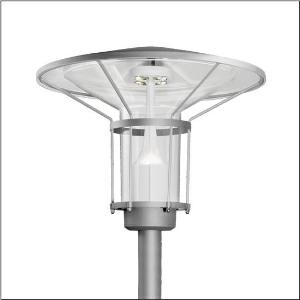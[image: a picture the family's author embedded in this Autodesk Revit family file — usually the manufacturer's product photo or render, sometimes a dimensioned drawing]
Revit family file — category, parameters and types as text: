
# Revit family: laterne_classic_iq___pl1_2s_5xa5245jf14h_d895
name_source: partatom
category: Lighting Fixtures
units: mm (PartAtom-declared; Revit-internal decimal feet)

## family parameters
Cut with Voids When Loaded = No
Host = Face
Light Source = No
Part Type = Normal
Room Calculation Point = No
Round Connector Dimension = Use Diameter
Shared = No

## types (1)
- --- (1 x LED, 2660 lm, 19.3 W, 3000K)
    Apparent Load = 19 VA
    CIE Flux Codes = 21 60 93 97 100
    Color Rendering = 70
    Color Temperature = 3000K
    Default Elevation = 1800 mm
    Description = Lantern Classic iQ, mast luminaire, Module 540 iQ-SR, primary light control with 3 zone facetted reflector, of plastic, silver coated, highly specular, structured, primary optical cover: cover, of PMMA, transparent, light distribution: PL1.2s, light emission: direct distribution, primary light characteristic: symmetric, installation type: post-top, LED, High Power LED, rated luminous flux: 2.670lm, luminous efficacy: 138lm/W, light colour: 730, colour temperature: 3000K, control gear: ECG iQ, control: Auto-Match, Temp-Guard, Lumen-Switch, Night-Set, Smart-Wire, Light-Fading, Desk-Remote (wireless, voltage-free reading and setting of iQ features in the workshop via application-optimized NFC function/RFID function), optimised constant luminous flux control (CLO 2.0), Street-Remote, presetting dimming logarithmic, with terminal, 6-pole, max. 2.5mm², mains connection: 230..240V, AC, 50/60Hz, start of lifetime: 19W, end of service life: 21W, reduction: 10W, luminaire housing, upper part, of glass-fibre reinforced polyester, coated, Siteco® metallic grey (DB 702S), diameter: 750mm, height: 596mm, spigot size: d x l = 76 x 70mm (post-top) | with reducer (optional accessory) 60 x 70mm, post-top mast mounting element, of diecast aluminium, coated, Siteco® metallic grey (DB 702S), Module 540 iQ-SR, traffic white (RAL 9016), equipment: standard, protection rating (complete): IP65, insulation class (complete): insulation class II (safety insulation), certification: CE, ENEC, VDE, packaging unit: 1 piece

Light Distribution: PL1.2s
    Height = 596 mm
    Lamp = 1 x LED
    Lamp Light Flux = 2660 lm
    Lamp Power = 19.3 W
    Lamp count = 1
    Length = 750 mm
    Luminous efficacy = 138 lm/W
    Manufacturer = Siteco
    ModVariant = No
    Model = 5XA5245JF14H
    Number of Poles = 1
    OnlyDefault = Yes
    Power Factor = 1
    Product Name = Laterne Classic iQ | PL1.2s
    Product group = mast luminaire | pylon top
    ProductGroupID = 6100
    Protection Class = Protection class II
    Protection Degree = IP 65
    RLX_Detail_Level = 1
    RLX_Emergency_Light_Flux = 0 lm
    RLX_Emergency_Type = 0
    RLX_Emergency_Type_DB = No
    RlxData = <blob elided: 62541 chars, md5=9557e2af>
    Socket = socket
    Standby Power = 0 W
    System Light Flux = 2660 lm
    System Power = 19 W
    Type Comments = factory setting: luminous flux: 100 % | dim-lin: 254 | 403 mA
    Type Image = l_1006052.jpg
    URL = http://relux.com
    VarID = @adj_095307
    Voltage = 0 V
    Weight = 0.00 kg
    Width = 0 mm  [stored 0 ft]

note: [stored X ft] marks values corroborated as IEEE doubles in the binary element streams (Revit-internal decimal feet)

## geometry (parser evidence)
native form markers: Blend x4, Sweep x9
no freeform markers — native parametric forms only
